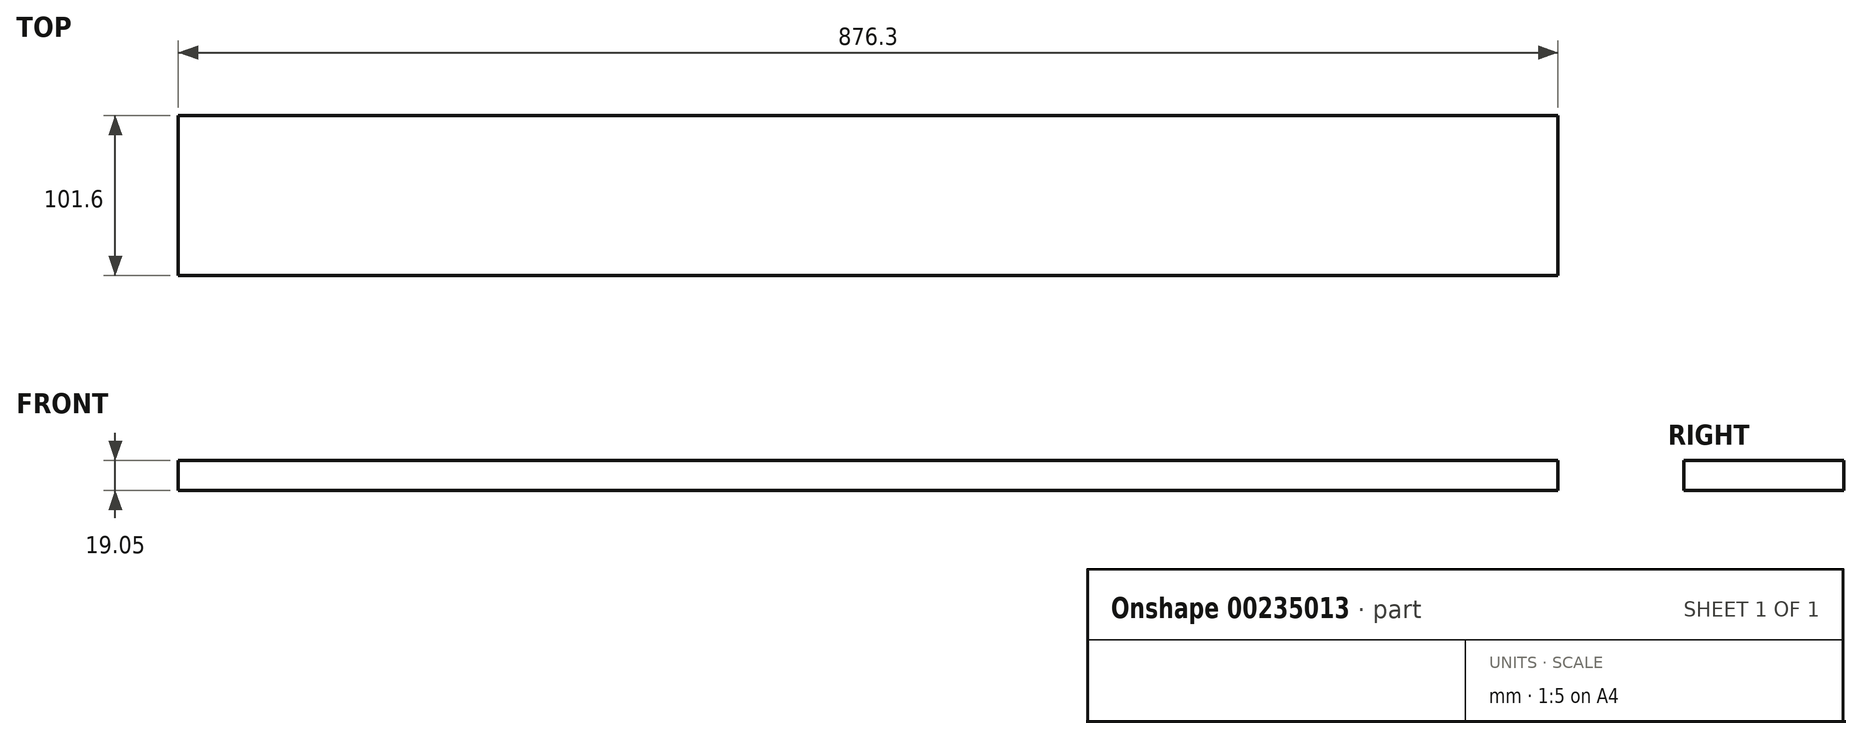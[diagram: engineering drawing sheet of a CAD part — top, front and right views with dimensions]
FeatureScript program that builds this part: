
annotation { "Feature Type Name" : "Feature", "Feature Type Description" : "" }
export const myFeature = defineFeature(function(context is Context, id is Id, definition is map)
    precondition{}
    {
        {
            var Q0;
            Q0=qCreatedBy(makeId("Top.planeOp"),FACE);
            var sketch = newSketch(context, id + "F0", { "sketchPlane" : qUnion([Q0])});
            skLineSegment(sketch, "E0.bottom", {"start": v(-438.15, 0) * mm, "end": v(438.15, 0) * mm});
            skLineSegment(sketch, "E0.top", {"start": v(-438.15, 101.6) * mm, "end": v(438.15, 101.6) * mm});
            skLineSegment(sketch, "E0.left", {"start": v(-438.15, 0) * mm, "end": v(-438.15, 101.6) * mm});
            skLineSegment(sketch, "E0.right", {"start": v(438.15, 0) * mm, "end": v(438.15, 101.6) * mm});
            skSolve(sketch);
        }
        {
            var Q0;
            Q0=makeQuery(id+"F0.imprint","IMPRINT",FACE,{"disambiguationData":[TD([[makeQuery(id+"F0.imprint","IMPRINT",EDGE,{"derivedFrom":sQuery(id+"F0.wireOp",EDGE,"E0.bottom")}),1.0]])]});
            extrude(context, id + "F1", {"entities" : qUnion([Q0]), "depth" : 19.05 * mm});
        }
    });
